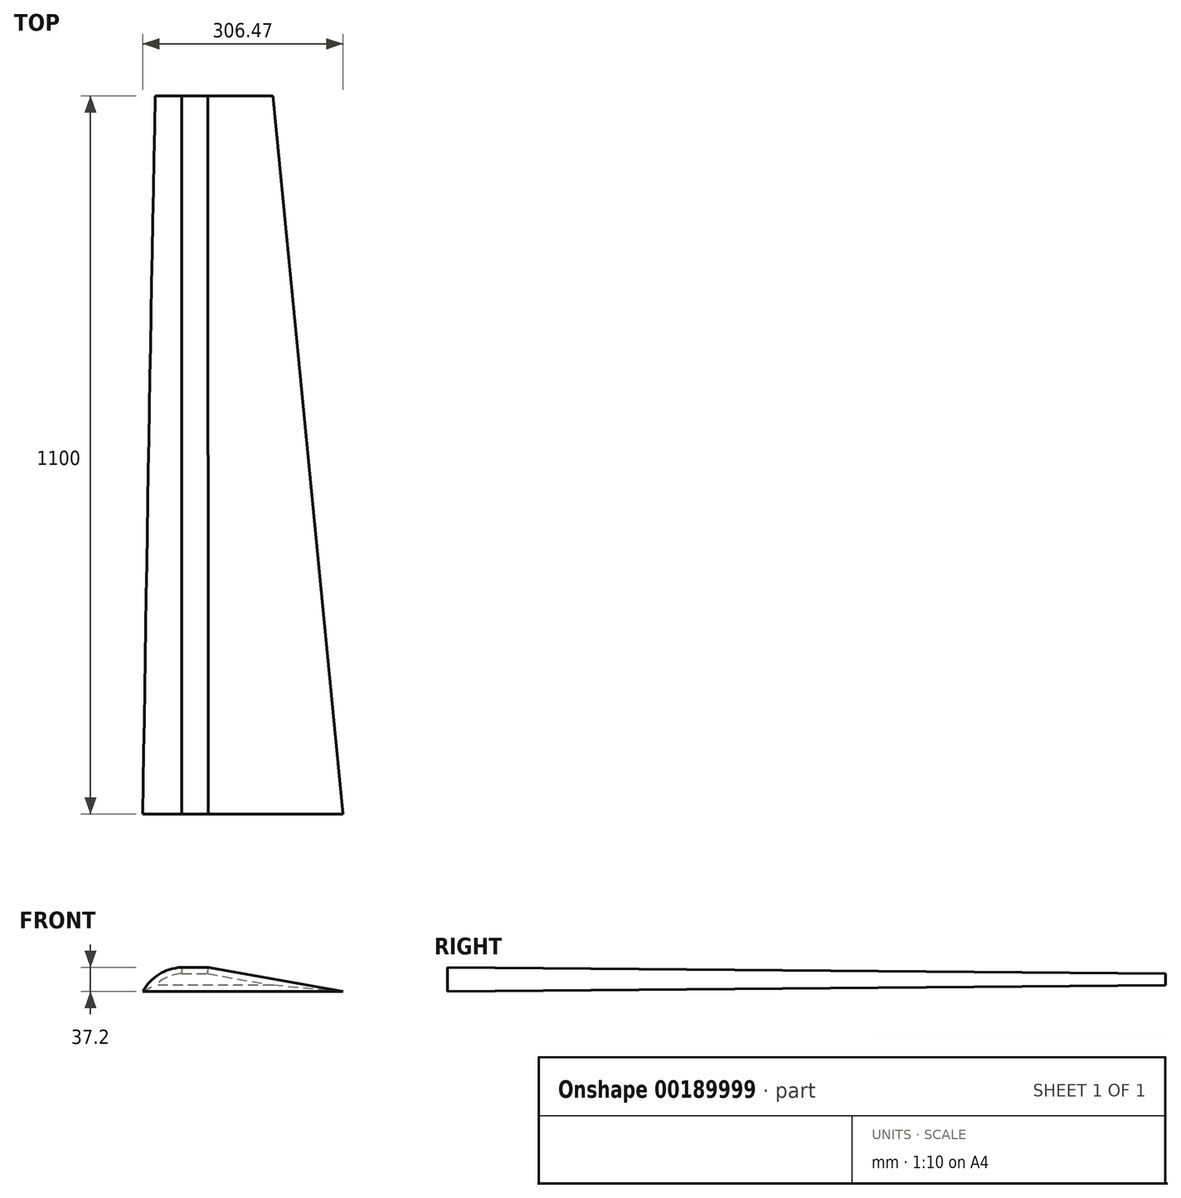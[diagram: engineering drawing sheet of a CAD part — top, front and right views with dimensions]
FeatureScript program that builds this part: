
annotation { "Feature Type Name" : "Feature", "Feature Type Description" : "" }
export const myFeature = defineFeature(function(context is Context, id is Id, definition is map)
    precondition{}
    {
        {
            var Q0;
            Q0=qCreatedBy(makeId("Front.planeOp"),FACE);
            var sketch = newSketch(context, id + "F0", { "sketchPlane" : qUnion([Q0])});
            skLineSegment(sketch, "E0.bottom", {"start": v(0, 0) * mm, "end": v(180, 0) * mm});
            skLineSegment(sketch, "E0.top", {"start": v(40.35, 18) * mm, "end": v(80.27, 18) * mm});
            skArc(sketch, "E1", {"start": v(40.35, 18) * mm, "mid": v(18.54, 12.66) * mm, "end": v(0, 0) * mm});
            skLineSegment(sketch, "E2", {"start": v(180, 0) * mm, "end": v(80.27, 18) * mm});
            skSolve(sketch);
        }
        {
            var Q0;
            Q0 = qSketchRegion(id + "F0", true);
            extrude(context, id + "F1", {"entities" : qUnion([Q0]), "depth" : 1100 * mm, "hasDraft" : true, "draftAngle" : 0.5 * degree});
        }
    });
